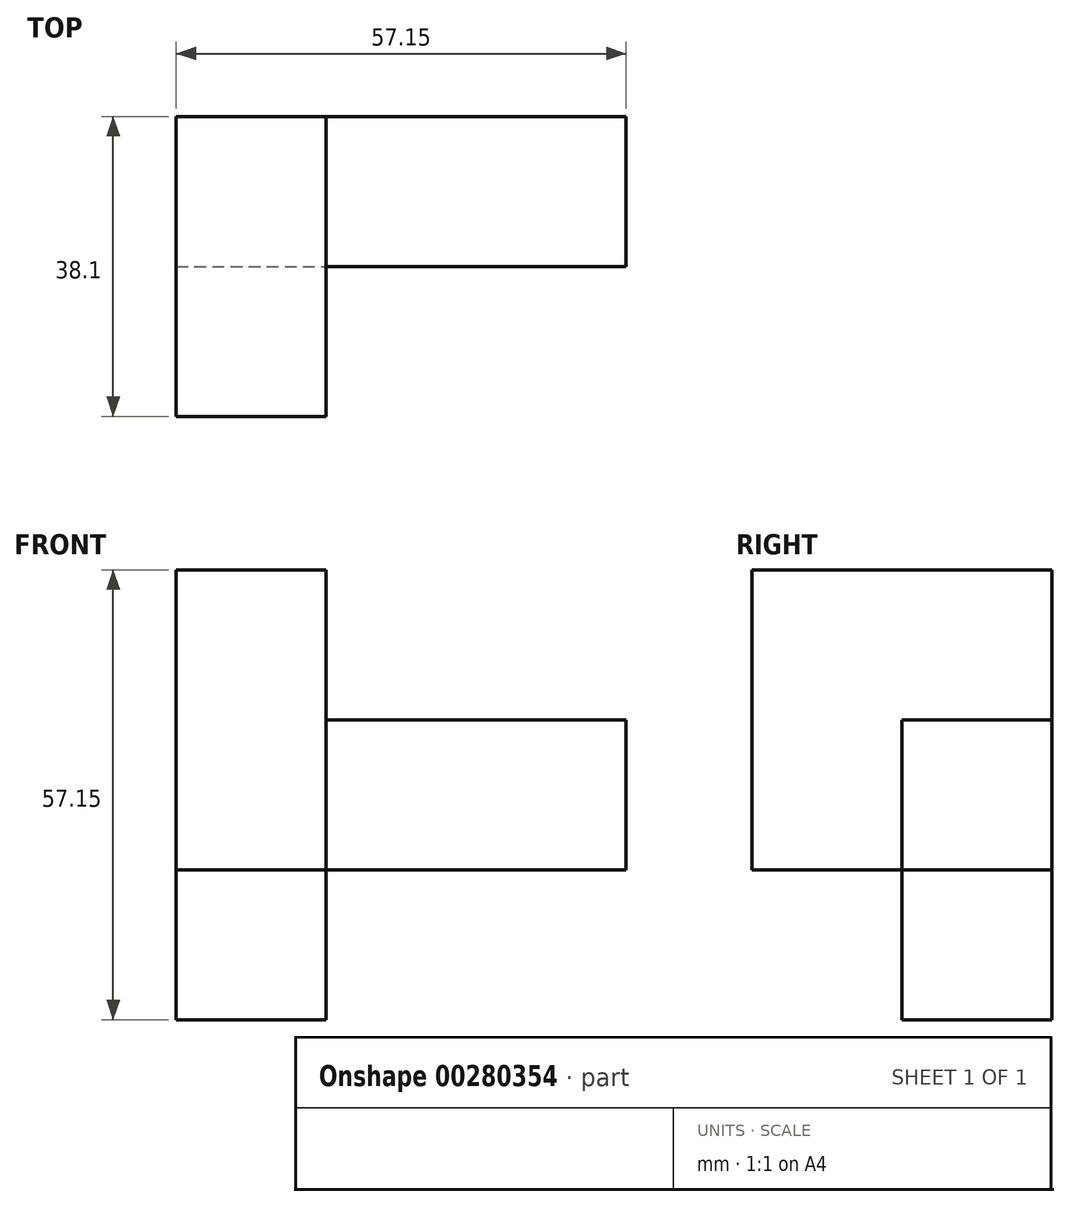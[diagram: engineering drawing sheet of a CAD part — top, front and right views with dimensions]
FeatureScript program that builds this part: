
annotation { "Feature Type Name" : "Feature", "Feature Type Description" : "" }
export const myFeature = defineFeature(function(context is Context, id is Id, definition is map)
    precondition{}
    {
        {
            var Q0;
            Q0=qCreatedBy(makeId("Top.planeOp"),FACE);
            var sketch = newSketch(context, id + "F0", { "sketchPlane" : qUnion([Q0])});
            skLineSegment(sketch, "E0.bottom", {"start": v(0, 0) * mm, "end": v(19.05, 0) * mm});
            skLineSegment(sketch, "E0.top", {"start": v(0, 38.1) * mm, "end": v(19.05, 38.1) * mm});
            skLineSegment(sketch, "E0.left", {"start": v(0, 0) * mm, "end": v(0, 38.1) * mm});
            skLineSegment(sketch, "E0.right", {"start": v(19.05, 0) * mm, "end": v(19.05, 38.1) * mm});
            skSolve(sketch);
        }
        {
            var Q0;
            Q0=makeQuery(id+"F0.imprint","IMPRINT",FACE,{"disambiguationData":[TD([[makeQuery(id+"F0.imprint","IMPRINT",EDGE,{"derivedFrom":sQuery(id+"F0.wireOp",EDGE,"E0.bottom")}),1.0]])]});
            extrude(context, id + "F1", {"entities" : qUnion([Q0]), "depth" : 57.15 * mm});
        }
        {
            var Q0;
            Q0=makeQuery(id+"F1.opExtrude","CAP_FACE",FACE,{"disambiguationData":[OSD([sQuery(id+"F0.wireOp",EDGE,"E0.bottom"),sQuery(id+"F0.wireOp",EDGE,"E0.top"),sQuery(id+"F0.wireOp",EDGE,"E0.left"),sQuery(id+"F0.wireOp",EDGE,"E0.right")])],"isStart":true});
            var sketch = newSketch(context, id + "F2", { "sketchPlane" : qUnion([Q0])});
            skLineSegment(sketch, "E1.bottom", {"start": v(0, 0) * mm, "end": v(19.05, 0) * mm});
            skLineSegment(sketch, "E1.top", {"start": v(0, -19.05) * mm, "end": v(19.05, -19.05) * mm});
            skLineSegment(sketch, "E1.left", {"start": v(0, 0) * mm, "end": v(0, -19.05) * mm});
            skLineSegment(sketch, "E1.right", {"start": v(19.05, 0) * mm, "end": v(19.05, -19.05) * mm});
            skSolve(sketch);
        }
        {
            var Q0;
            Q0 = qSketchRegion(id + "F2", true);
            extrude(context, id + "F3", {"entities" : qUnion([Q0]), "operationType" : NewBodyOperationType.REMOVE, "oppositeDirection" : true, "depth" : 19.05 * mm});
        }
        {
            var Q0;
            Q0=makeQuery(id+"F1.opExtrude","SWEPT_FACE",FACE,{"disambiguationData":[OSD([sQuery(id+"F0.wireOp",EDGE,"E0.right")])]});
            var sketch = newSketch(context, id + "F4", { "sketchPlane" : qUnion([Q0])});
            skLineSegment(sketch, "E2.bottom", {"start": v(19.05, 19.05) * mm, "end": v(38.1, 19.05) * mm});
            skLineSegment(sketch, "E2.top", {"start": v(19.05, 38.1) * mm, "end": v(38.1, 38.1) * mm});
            skLineSegment(sketch, "E2.left", {"start": v(19.05, 19.05) * mm, "end": v(19.05, 38.1) * mm});
            skLineSegment(sketch, "E2.right", {"start": v(38.1, 19.05) * mm, "end": v(38.1, 38.1) * mm});
            skSolve(sketch);
        }
        {
            var Q0;
            Q0 = qSketchRegion(id + "F4", true);
            extrude(context, id + "F5", {"entities" : qUnion([Q0]), "operationType" : NewBodyOperationType.ADD, "depth" : 38.1 * mm});
        }
    });
